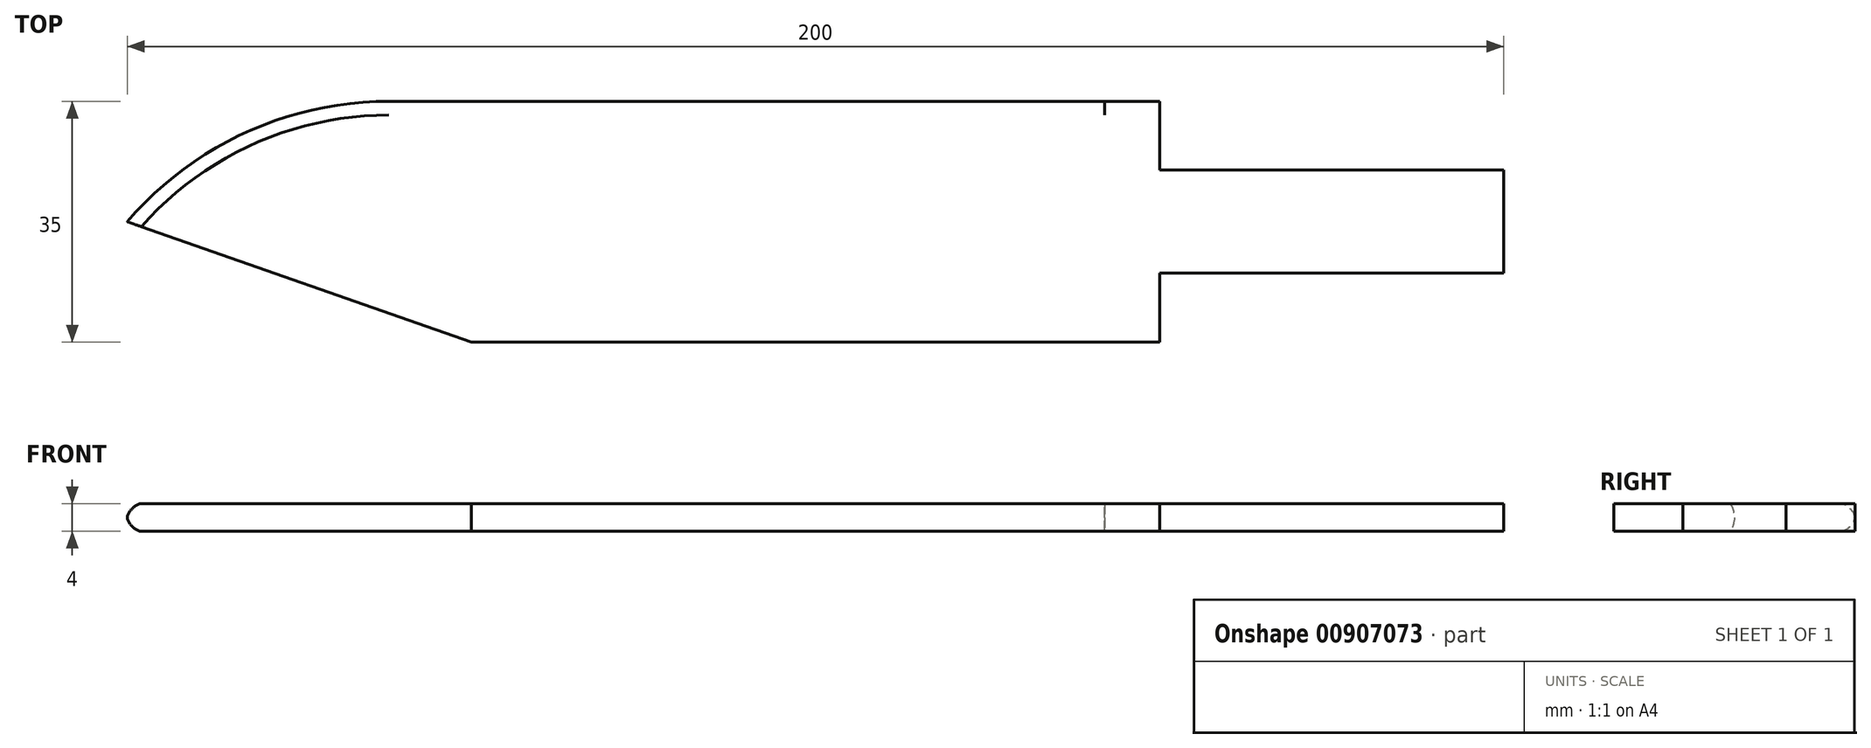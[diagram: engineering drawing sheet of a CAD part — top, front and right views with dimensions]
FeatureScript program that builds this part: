
annotation { "Feature Type Name" : "Feature", "Feature Type Description" : "" }
export const myFeature = defineFeature(function(context is Context, id is Id, definition is map)
    precondition{}
    {
        {
            var Q0;
            Q0=qCreatedBy(makeId("Top.planeOp"),FACE);
            var sketch = newSketch(context, id + "F0", { "sketchPlane" : qUnion([Q0])});
            skLineSegment(sketch, "E0.bottom", {"start": v(75, 17.5) * mm, "end": v(-37, 17.5) * mm});
            skLineSegment(sketch, "E0.top", {"start": v(75, -17.5) * mm, "end": v(-25, -17.5) * mm});
            skLineSegment(sketch, "E0.left", {"start": v(75, 17.5) * mm, "end": v(75, 7.5) * mm});
            skPoint(sketch, "E0.middle", {"position": v(0, 0) * mm});
            skLineSegment(sketch, "E1.bottom", {"start": v(75, 7.5) * mm, "end": v(125, 7.5) * mm});
            skLineSegment(sketch, "E1.top", {"start": v(75, -7.5) * mm, "end": v(125, -7.5) * mm});
            skLineSegment(sketch, "E1.right", {"start": v(125, 7.5) * mm, "end": v(125, -7.5) * mm});
            skArc(sketch, "E2", {"start": v(-37, 17.5) * mm, "mid": v(-57.92, 12.91) * mm, "end": v(-75, 0) * mm});
            skLineSegment(sketch, "E3", {"start": v(-75, 0) * mm, "end": v(-25, -17.5) * mm});
            skPoint(sketch, "E4.orphan", {"position": v(-75, 17.5) * mm});
            skPoint(sketch, "E5.orphan", {"position": v(-75, -17.5) * mm});
            skLineSegment(sketch, "E6.trimOffspring", {"start": v(75, -7.5) * mm, "end": v(75, -17.5) * mm});
            skSolve(sketch);
        }
        {
            var Q0;
            Q0 = qSketchRegion(id + "F0", true);
            extrude(context, id + "F1", {"entities" : qUnion([Q0]), "depth" : 4 * mm, "offsetDistance" : 25 * mm});
        }
        {
            var Q0;
            Q0=makeQuery(id+"F1.opExtrude","SWEPT_FACE",FACE,{"disambiguationData":[OSD([sQuery(id+"F0.wireOp",EDGE,"E0.bottom")])]});
            var sketch = newSketch(context, id + "F2", { "sketchPlane" : qUnion([Q0])});
            skLineSegment(sketch, "E7.bottom", {"start": v(-75, 4) * mm, "end": v(-67, 4) * mm});
            skLineSegment(sketch, "E7.top", {"start": v(-75, 0) * mm, "end": v(-67, 0) * mm});
            skLineSegment(sketch, "E7.left", {"start": v(-75, 4) * mm, "end": v(-75, 0) * mm});
            skLineSegment(sketch, "E7.right", {"start": v(-67, 4) * mm, "end": v(-67, 0) * mm});
            skSolve(sketch);
        }
        {
            var Q0;
            Q0 = qSketchRegion(id + "F2", true);
            extrude(context, id + "F3", {"entities" : qUnion([Q0]), "operationType" : NewBodyOperationType.ADD, "depth" : 0.5 * mm, "offsetDistance" : 25 * mm});
        }
        {
            var Q0;
            Q0=makeQuery(id+"F1.opExtrude","CAP_EDGE",EDGE,{"disambiguationData":[OSD([sQuery(id+"F0.wireOp",EDGE,"E0.bottom")])],"isStart":false});
            var Q1;
            Q1=makeQuery(id+"F1.opExtrude","CAP_EDGE",EDGE,{"disambiguationData":[OSD([sQuery(id+"F0.wireOp",EDGE,"E0.bottom")])],"isStart":true});
            fillet(context, id + "F4", {"entities" : qUnion([Q0, Q1]), "radius" : 2 * mm, "tangentPropagation" : true, "rho" : 0.3, "crossSection" : FilletCrossSection.CONIC, "allowEdgeOverflow" : false});
        }
        {
            var Q0;
            Q0=makeQuery(id+"F3.opExtrude","CAP_FACE",FACE,{"disambiguationData":[OSD([sQuery(id+"F2.wireOp",EDGE,"E7.bottom"),sQuery(id+"F2.wireOp",EDGE,"E7.top"),sQuery(id+"F2.wireOp",EDGE,"E7.left"),sQuery(id+"F2.wireOp",EDGE,"E7.right")])],"isStart":false});
            var sketch = newSketch(context, id + "F5", { "sketchPlane" : qUnion([Q0])});
            skLineSegment(sketch, "E8.bottom", {"start": v(-75, 4) * mm, "end": v(-67, 4) * mm});
            skLineSegment(sketch, "E8.top", {"start": v(-75, 0) * mm, "end": v(-67, 0) * mm});
            skLineSegment(sketch, "E8.left", {"start": v(-75, 4) * mm, "end": v(-75, 0) * mm});
            skLineSegment(sketch, "E8.right", {"start": v(-67, 4) * mm, "end": v(-67, 0) * mm});
            skSolve(sketch);
        }
        {
            var Q0;
            Q0 = qSketchRegion(id + "F5", true);
            extrude(context, id + "F6", {"entities" : qUnion([Q0]), "operationType" : NewBodyOperationType.REMOVE, "oppositeDirection" : true, "depth" : 0.5 * mm, "offsetDistance" : 25 * mm});
        }
    });
